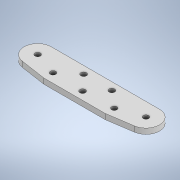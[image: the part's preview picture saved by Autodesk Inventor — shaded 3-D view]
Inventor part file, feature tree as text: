
AUTODESK INVENTOR PART (.ipt)
format: ipt  version: 2020 (Build 240168000, 168)  size: 133,120 bytes
history: native  units: in
note: dims shown in document units (in); Inventor stores cm internally (conversion verified against a paired STEP export)
features: extrude x1, sketch x1
ambient origin geometry x8: Origin, YZ Plane, XZ Plane, XY Plane, X Axis, Y Axis, Z Axis, Center Point
bodies: Solid1 (feature_tree)
feature tree (2):
  extrude  "Extrusion1"  Depth=0.1181in TaperAngle=0.0deg
  sketch  "Sketch1"  dims[d0=0.3937in d1=0.3937in d2=0.5906in d3=0.5906in d4=0.122in d5=0.122in d6=0.122in d7=0.1181in d8=0.0in]
